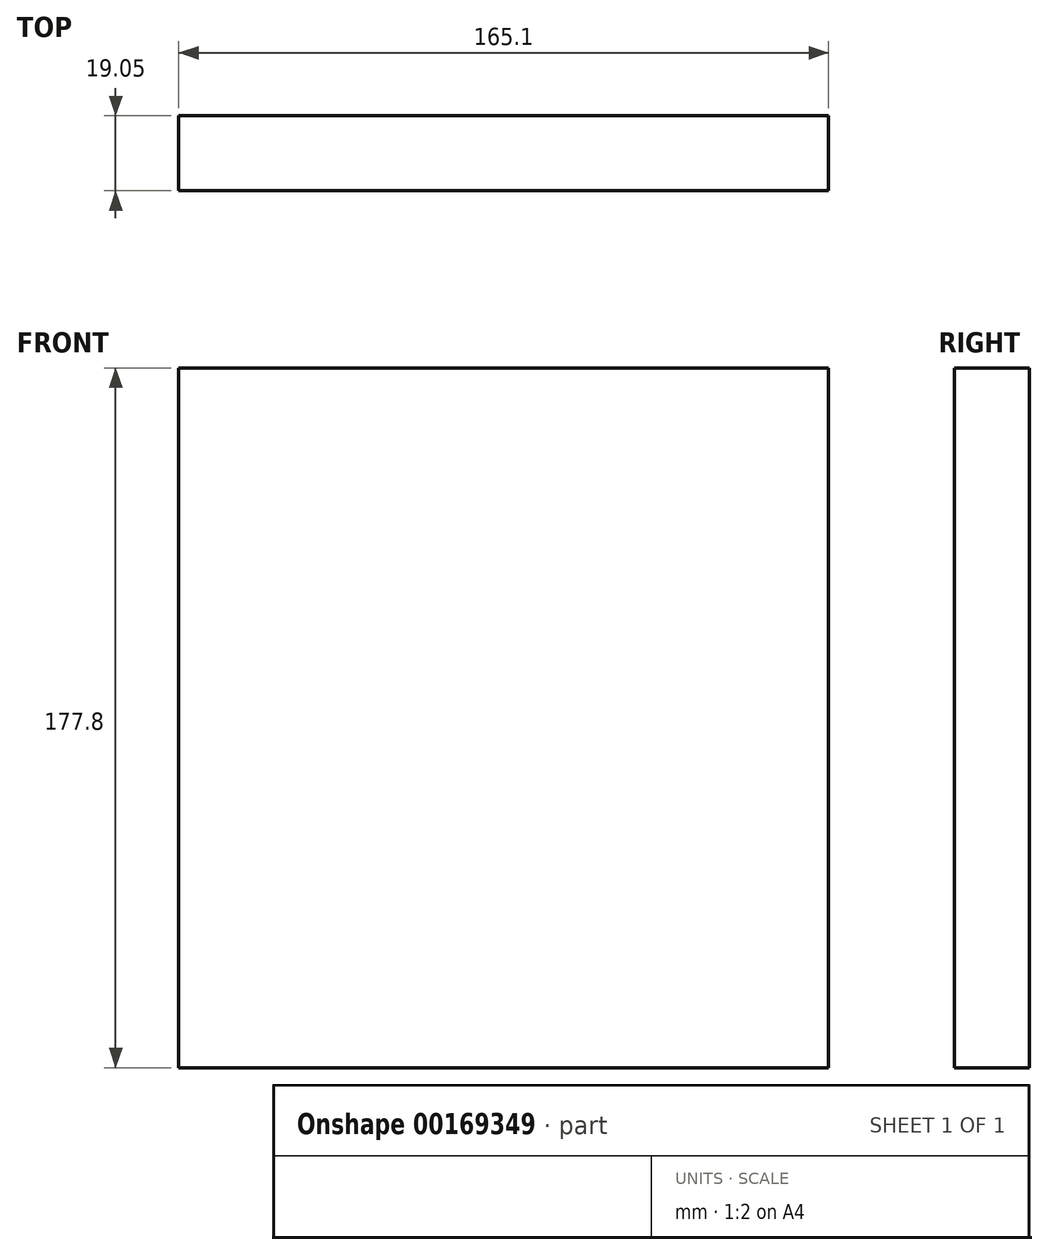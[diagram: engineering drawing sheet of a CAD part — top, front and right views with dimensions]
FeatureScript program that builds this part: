
annotation { "Feature Type Name" : "Feature", "Feature Type Description" : "" }
export const myFeature = defineFeature(function(context is Context, id is Id, definition is map)
    precondition{}
    {
        {
            var Q0;
            Q0=qCreatedBy(makeId("Front.planeOp"),FACE);
            var sketch = newSketch(context, id + "F0", { "sketchPlane" : qUnion([Q0])});
            skLineSegment(sketch, "E0.bottom", {"start": v(0, 0) * mm, "end": v(165.1, 0) * mm});
            skLineSegment(sketch, "E0.top", {"start": v(0, 44.45) * mm, "end": v(165.1, 44.45) * mm});
            skLineSegment(sketch, "E0.left", {"start": v(0, 0) * mm, "end": v(0, 44.45) * mm});
            skLineSegment(sketch, "E0.right", {"start": v(165.1, 0) * mm, "end": v(165.1, 44.45) * mm});
            skLineSegment(sketch, "E1.top", {"start": v(0, 88.9) * mm, "end": v(165.1, 88.9) * mm});
            skLineSegment(sketch, "E1.left", {"start": v(0, 44.45) * mm, "end": v(0, 88.9) * mm});
            skLineSegment(sketch, "E1.right", {"start": v(165.1, 44.45) * mm, "end": v(165.1, 88.9) * mm});
            skLineSegment(sketch, "E2.top", {"start": v(0, 133.35) * mm, "end": v(165.1, 133.35) * mm});
            skLineSegment(sketch, "E2.left", {"start": v(0, 88.9) * mm, "end": v(0, 133.35) * mm});
            skLineSegment(sketch, "E2.right", {"start": v(165.1, 88.9) * mm, "end": v(165.1, 133.35) * mm});
            skLineSegment(sketch, "E3.top", {"start": v(0, 177.8) * mm, "end": v(165.1, 177.8) * mm});
            skLineSegment(sketch, "E3.left", {"start": v(0, 133.35) * mm, "end": v(0, 177.8) * mm});
            skLineSegment(sketch, "E3.right", {"start": v(165.1, 133.35) * mm, "end": v(165.1, 177.8) * mm});
            skLineSegment(sketch, "E4.bottom", {"start": v(0, 177.8) * mm, "end": v(660.4, 177.8) * mm});
            skSolve(sketch);
        }
        {
            var Q0;
            Q0=makeQuery(id+"F0.imprint","IMPRINT",FACE,{"disambiguationData":[TD([[makeQuery(id+"F0.imprint","IMPRINT",EDGE,{"derivedFrom":sQuery(id+"F0.wireOp",EDGE,"E2.top")}),1.0]])]});
            var Q1;
            Q1=makeQuery(id+"F0.imprint","IMPRINT",FACE,{"disambiguationData":[TD([[makeQuery(id+"F0.imprint","IMPRINT",EDGE,{"derivedFrom":sQuery(id+"F0.wireOp",EDGE,"E1.top")}),1.0]])]});
            var Q2;
            Q2=makeQuery(id+"F0.imprint","IMPRINT",FACE,{"disambiguationData":[TD([[makeQuery(id+"F0.imprint","IMPRINT",EDGE,{"derivedFrom":sQuery(id+"F0.wireOp",EDGE,"E0.top")}),1.0]])]});
            var Q3;
            Q3=makeQuery(id+"F0.imprint","IMPRINT",FACE,{"disambiguationData":[TD([[makeQuery(id+"F0.imprint","IMPRINT",EDGE,{"derivedFrom":sQuery(id+"F0.wireOp",EDGE,"E0.bottom")}),1.0]])]});
            extrude(context, id + "F1", {"entities" : qUnion([Q0, Q1, Q2, Q3]), "oppositeDirection" : true, "depth" : 19.05 * mm});
        }
    });
